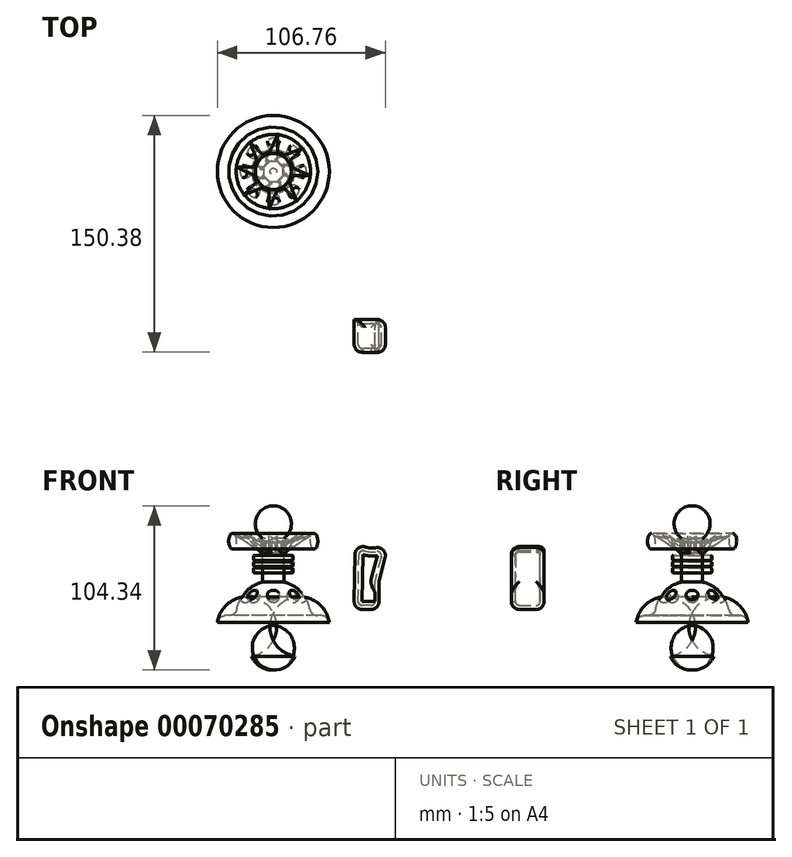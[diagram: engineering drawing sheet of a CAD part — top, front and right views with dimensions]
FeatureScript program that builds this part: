
annotation { "Feature Type Name" : "Feature", "Feature Type Description" : "" }
export const myFeature = defineFeature(function(context is Context, id is Id, definition is map)
    precondition{}
    {
        {
            var Q0;
            Q0=qCreatedBy(makeId("Front.planeOp"),FACE);
            var sketch = newSketch(context, id + "F0", { "sketchPlane" : qUnion([Q0])});
            skLineSegment(sketch, "E0", {"start": v(0, 56) * mm, "end": v(6.7, 56) * mm});
            skLineSegment(sketch, "E1", {"start": v(6.7, 56) * mm, "end": v(6.7, 21.36) * mm});
            skArc(sketch, "E2", {"start": v(23.55, 0) * mm, "mid": v(18.85, 13.62) * mm, "end": v(6.7, 21.36) * mm});
            skLineSegment(sketch, "E3", {"start": v(23.55, 0) * mm, "end": v(34.4, 0) * mm});
            skArc(sketch, "E4", {"start": v(13.85, -25.75) * mm, "mid": v(31.62, -18.85) * mm, "end": v(34.4, 0) * mm});
            skArc(sketch, "E5", {"start": v(0, -34.52) * mm, "mid": v(8.33, -32.35) * mm, "end": v(13.85, -25.75) * mm});
            skLineSegment(sketch, "E6", {"start": v(0, 54.15) * mm, "end": v(0, -34.52) * mm});
            skLineSegment(sketch, "E7", {"start": v(0, 54.15) * mm, "end": v(0, 56) * mm});
            skSolve(sketch);
        }
        {
            var Q0;
            Q0=makeQuery(id+"F0.imprint","IMPRINT",FACE,{"disambiguationData":[TD([[makeQuery(id+"F0.imprint","IMPRINT",EDGE,{"derivedFrom":sQuery(id+"F0.wireOp",EDGE,"E0")}),-1.0]])]});
            var Q1;
            Q1=sQuery(id+"F0.wireOp",EDGE,"E6");
            revolve(context, id + "F1", {"entities" : qUnion([Q0]), "axis" : qUnion([Q1]), "revolveType" : RevolveType.FULL});
        }
        {
            var Q0;
            Q0=makeQuery(id+"F1.opRevolve","SWEPT_EDGE",EDGE,{"disambiguationData":[OSD([sQuery(id+"F0.wireOp",EDGE,"E2"),sQuery(id+"F0.wireOp",EDGE,"E3")])]});
            var Q1;
            Q1=makeQuery(id+"F1.opRevolve","SWEPT_EDGE",EDGE,{"disambiguationData":[OSD([sQuery(id+"F0.wireOp",EDGE,"E3"),sQuery(id+"F0.wireOp",EDGE,"E4")])]});
            fillet(context, id + "F2", {"entities" : qUnion([Q0, Q1]), "radius" : 5.08 * mm, "tangentPropagation" : true, "allowEdgeOverflow" : false});
        }
        {
            var Q0;
            Q0=qCreatedBy(makeId("Front.planeOp"),FACE);
            cPlane(context, id + "F3", {"entities" : qUnion([Q0]), "cplaneType" : CPlaneType.OFFSET, "offset" : 76.2 * mm, "width" : 152.4 * mm, "height" : 152.4 * mm});
        }
        {
            var Q0;
            Q0=qCreatedBy(id+"F3.planeOp",FACE);
            var sketch = newSketch(context, id + "F4", { "sketchPlane" : qUnion([Q0])});
            skCircle(sketch, "E8", {"center": v(0, 12.35) * mm, "radius": 4.03 * mm});
            skLineSegment(sketch, "E9", {"start": v(0, 16.39) * mm, "end": v(0, 8.32) * mm});
            skSolve(sketch);
        }
        {
            var Q0;
            {var subQ0=sQuery(id+"F4.wireOp",EDGE,"E9");Q0=makeQuery(id+"F4.imprint","IMPRINT",FACE,{"disambiguationData":[TD([[makeQuery(id+"F4.imprint","IMPRINT",EDGE,{"derivedFrom":subQ0}),1.0]])]});}
            var Q1;
            Q1=sQuery(id+"F4.wireOp",EDGE,"E9");
            revolve(context, id + "F5", {"entities" : qUnion([Q0]), "axis" : qUnion([Q1]), "revolveType" : RevolveType.FULL});
        }
        {
            var Q0;
            Q0=makeQuery(id+"F5.opRevolve","SWEPT_BODY",BODY,{"disambiguationData":[OSD([sQuery(id+"F4.wireOp",EDGE,"E8"),sQuery(id+"F4.wireOp",EDGE,"E9")])]});
            transform(context, id + "F6", {"entities" : qUnion([Q0]), "transformType" : TransformType.TRANSLATION_3D, "dx" : 0 * mm, "dy" : 58.43 * mm, "dz" : 0 * mm, "makeCopy" : false});
        }
        {
            var Q0;
            Q0=qCreatedBy(makeId("Top.planeOp"),FACE);
            cPlane(context, id + "F7", {"entities" : qUnion([Q0]), "cplaneType" : CPlaneType.OFFSET, "offset" : 152.4 * mm, "width" : 152.4 * mm, "height" : 152.4 * mm});
        }
        {
            var Q0;
            Q0=qCreatedBy(id+"F7.planeOp",FACE);
            var sketch = newSketch(context, id + "F8", { "sketchPlane" : qUnion([Q0])});
            skCircle(sketch, "E10", {"center": v(0, 0) * mm, "radius": 11.45 * mm});
            skLineSegment(sketch, "E11", {"start": v(0, 11.45) * mm, "end": v(0, -11.45) * mm});
            skSolve(sketch);
        }
        {
            var Q0;
            {var subQ0=sQuery(id+"F8.wireOp",EDGE,"E11");Q0=makeQuery(id+"F8.imprint","IMPRINT",FACE,{"disambiguationData":[TD([[makeQuery(id+"F8.imprint","IMPRINT",EDGE,{"derivedFrom":subQ0}),1.0]])]});}
            var Q1;
            Q1=sQuery(id+"F8.wireOp",EDGE,"E11");
            revolve(context, id + "F9", {"entities" : qUnion([Q0]), "axis" : qUnion([Q1]), "revolveType" : RevolveType.FULL});
        }
        {
            var Q0;
            Q0=makeQuery(id+"F9.opRevolve","SWEPT_BODY",BODY,{"disambiguationData":[OSD([sQuery(id+"F8.wireOp",EDGE,"E10"),sQuery(id+"F8.wireOp",EDGE,"E11")])]});
            transform(context, id + "F10", {"entities" : qUnion([Q0]), "transformType" : TransformType.TRANSLATION_3D, "dx" : 0 * mm, "dy" : 0 * mm, "dz" : -94.04 * mm, "makeCopy" : false});
        }
        {
            var Q0;
            Q0=makeQuery(id+"F9.opRevolve","SWEPT_BODY",BODY,{"disambiguationData":[OSD([sQuery(id+"F8.wireOp",EDGE,"E10"),sQuery(id+"F8.wireOp",EDGE,"E11")])]});
            var Q1;
            Q1=makeQuery(id+"F1.opRevolve","SWEPT_BODY",BODY,{"disambiguationData":[OSD([sQuery(id+"F0.wireOp",EDGE,"E0"),sQuery(id+"F0.wireOp",EDGE,"E1"),sQuery(id+"F0.wireOp",EDGE,"E2"),sQuery(id+"F0.wireOp",EDGE,"E3"),sQuery(id+"F0.wireOp",EDGE,"E4"),sQuery(id+"F0.wireOp",EDGE,"E5"),sQuery(id+"F0.wireOp",EDGE,"E6"),sQuery(id+"F0.wireOp",EDGE,"E7")])]});
            booleanBodies(context, id + "F11", {"operationType" : BooleanOperationType.UNION, "tools" : qUnion([Q0, Q1])});
        }
        {
            var Q0;
            Q0=makeQuery(id+"F5.opRevolve","SWEPT_BODY",BODY,{"disambiguationData":[OSD([sQuery(id+"F4.wireOp",EDGE,"E8"),sQuery(id+"F4.wireOp",EDGE,"E9")])]});
            var Q1;
            Q1=makeQuery(id+"F1.opRevolve","SWEPT_EDGE",EDGE,{"disambiguationData":[OSD([sQuery(id+"F0.wireOp",EDGE,"E1"),sQuery(id+"F0.wireOp",EDGE,"E2")])]});
            circularPattern(context, id + "F12", {"entities" : qUnion([Q0]), "axis" : qUnion([Q1]), "angle" : 360 * degree, "instanceCount" : 8, "equalSpace" : true});
        }
        {
            var Q0;
            Q0=makeQuery(id+"F5.opRevolve","SWEPT_BODY",BODY,{"disambiguationData":[OSD([sQuery(id+"F4.wireOp",EDGE,"E8"),sQuery(id+"F4.wireOp",EDGE,"E9")])]});
            var Q1;
            Q1=makeQuery(id+"F9.opRevolve","SWEPT_BODY",BODY,{"disambiguationData":[OSD([sQuery(id+"F8.wireOp",EDGE,"E10"),sQuery(id+"F8.wireOp",EDGE,"E11")])]});
            booleanBodies(context, id + "F13", {"operationType" : BooleanOperationType.SUBTRACTION, "tools" : qUnion([Q0]), "targets" : qUnion([Q1])});
        }
        {
            var Q0;
            Q0=makeQuery(id+"F12.opPattern","COPY",BODY,{"derivedFrom":makeQuery(id+"F5.opRevolve","SWEPT_BODY",BODY,{"disambiguationData":[OSD([sQuery(id+"F4.wireOp",EDGE,"E8"),sQuery(id+"F4.wireOp",EDGE,"E9")])]}),"instanceName":"1"});
            var Q1;
            Q1=makeQuery(id+"F9.opRevolve","SWEPT_BODY",BODY,{"disambiguationData":[OSD([sQuery(id+"F8.wireOp",EDGE,"E10"),sQuery(id+"F8.wireOp",EDGE,"E11")])]});
            booleanBodies(context, id + "F14", {"operationType" : BooleanOperationType.SUBTRACTION, "tools" : qUnion([Q0]), "targets" : qUnion([Q1])});
        }
        {
            var Q0;
            Q0=makeQuery(id+"F12.opPattern","COPY",BODY,{"derivedFrom":makeQuery(id+"F5.opRevolve","SWEPT_BODY",BODY,{"disambiguationData":[OSD([sQuery(id+"F4.wireOp",EDGE,"E8"),sQuery(id+"F4.wireOp",EDGE,"E9")])]}),"instanceName":"2"});
            var Q1;
            Q1=makeQuery(id+"F9.opRevolve","SWEPT_BODY",BODY,{"disambiguationData":[OSD([sQuery(id+"F8.wireOp",EDGE,"E10"),sQuery(id+"F8.wireOp",EDGE,"E11")])]});
            booleanBodies(context, id + "F15", {"operationType" : BooleanOperationType.SUBTRACTION, "tools" : qUnion([Q0]), "targets" : qUnion([Q1])});
        }
        {
            var Q0;
            Q0=makeQuery(id+"F12.opPattern","COPY",BODY,{"derivedFrom":makeQuery(id+"F5.opRevolve","SWEPT_BODY",BODY,{"disambiguationData":[OSD([sQuery(id+"F4.wireOp",EDGE,"E8"),sQuery(id+"F4.wireOp",EDGE,"E9")])]}),"instanceName":"3"});
            var Q1;
            Q1=makeQuery(id+"F12.opPattern","COPY",BODY,{"derivedFrom":makeQuery(id+"F5.opRevolve","SWEPT_BODY",BODY,{"disambiguationData":[OSD([sQuery(id+"F4.wireOp",EDGE,"E8"),sQuery(id+"F4.wireOp",EDGE,"E9")])]}),"instanceName":"4"});
            var Q2;
            Q2=makeQuery(id+"F12.opPattern","COPY",BODY,{"derivedFrom":makeQuery(id+"F5.opRevolve","SWEPT_BODY",BODY,{"disambiguationData":[OSD([sQuery(id+"F4.wireOp",EDGE,"E8"),sQuery(id+"F4.wireOp",EDGE,"E9")])]}),"instanceName":"5"});
            var Q3;
            Q3=makeQuery(id+"F12.opPattern","COPY",BODY,{"derivedFrom":makeQuery(id+"F5.opRevolve","SWEPT_BODY",BODY,{"disambiguationData":[OSD([sQuery(id+"F4.wireOp",EDGE,"E8"),sQuery(id+"F4.wireOp",EDGE,"E9")])]}),"instanceName":"6"});
            var Q4;
            Q4=makeQuery(id+"F12.opPattern","COPY",BODY,{"derivedFrom":makeQuery(id+"F5.opRevolve","SWEPT_BODY",BODY,{"disambiguationData":[OSD([sQuery(id+"F4.wireOp",EDGE,"E8"),sQuery(id+"F4.wireOp",EDGE,"E9")])]}),"instanceName":"7"});
            var Q5;
            Q5=makeQuery(id+"F9.opRevolve","SWEPT_BODY",BODY,{"disambiguationData":[OSD([sQuery(id+"F8.wireOp",EDGE,"E10"),sQuery(id+"F8.wireOp",EDGE,"E11")])]});
            booleanBodies(context, id + "F16", {"operationType" : BooleanOperationType.SUBTRACTION, "tools" : qUnion([Q0, Q1, Q2, Q3, Q4]), "targets" : qUnion([Q5])});
        }
        {
            var Q0;
            Q0=qCreatedBy(makeId("Front.planeOp"),FACE);
            var sketch = newSketch(context, id + "F17", { "sketchPlane" : qUnion([Q0])});
            skEllipse(sketch, "E12", {"center": v(-25.95, 47.27) * mm, "majorRadius": 2.35 * mm, "minorRadius": 4.94 * mm, "majorAxis": v(1, 0)});
            skSolve(sketch);
        }
        {
            var Q0;
            Q0=makeQuery(id+"F17.imprint","IMPRINT",FACE,{"disambiguationData":[TD([[makeQuery(id+"F17.imprint","IMPRINT",EDGE,{"derivedFrom":sQuery(id+"F17.wireOp",EDGE,"E12")}),1.0]])]});
            var Q1;
            Q1=makeQuery(id+"F11.opBoolean","INTERSECT",EDGE,{"derivedFrom":[makeQuery(id+"F1.opRevolve","SWEPT_FACE",FACE,{"disambiguationData":[OSD([sQuery(id+"F0.wireOp",EDGE,"E1")])]}),makeQuery(id+"F9.opRevolve","SWEPT_FACE",FACE,{"disambiguationData":[OSD([sQuery(id+"F8.wireOp",EDGE,"E10")])]})]});
            sweep(context, id + "F18", {"profiles" : qUnion([Q0]), "path" : qUnion([Q1])});
        }
        {
            var Q0;
            Q0=qCreatedBy(makeId("Front.planeOp"),FACE);
            var sketch = newSketch(context, id + "F19", { "sketchPlane" : qUnion([Q0])});
            skEllipse(sketch, "E13", {"center": v(-12.17, 36.73) * mm, "majorRadius": 1.54 * mm, "minorRadius": 0.39 * mm, "majorAxis": v(0, 1)});
            skSolve(sketch);
        }
        {
            var Q0;
            Q0=makeQuery(id+"F19.imprint","IMPRINT",FACE,{"disambiguationData":[TD([[makeQuery(id+"F19.imprint","IMPRINT",EDGE,{"derivedFrom":sQuery(id+"F19.wireOp",EDGE,"E13")}),1.0]])]});
            var Q1;
            Q1=makeQuery(id+"F1.opRevolve","SWEPT_EDGE",EDGE,{"disambiguationData":[OSD([sQuery(id+"F0.wireOp",EDGE,"E1"),sQuery(id+"F0.wireOp",EDGE,"E2")])]});
            sweep(context, id + "F20", {"profiles" : qUnion([Q0]), "path" : qUnion([Q1])});
        }
        {
            var Q0;
            Q0=makeQuery(id+"F20.opSweep","SWEPT_BODY",BODY,{"disambiguationData":[OSD([sQuery(id+"F0.wireOp",EDGE,"E1"),sQuery(id+"F0.wireOp",EDGE,"E2"),sQuery(id+"F19.wireOp",EDGE,"E13")])]});
            transform(context, id + "F21", {"entities" : qUnion([Q0]), "transformType" : TransformType.COPY});
        }
        {
            var Q0;
            Q0=makeQuery(id+"F20.opSweep","SWEPT_BODY",BODY,{"disambiguationData":[OSD([sQuery(id+"F0.wireOp",EDGE,"E1"),sQuery(id+"F0.wireOp",EDGE,"E2"),sQuery(id+"F19.wireOp",EDGE,"E13")])]});
            transform(context, id + "F22", {"entities" : qUnion([Q0]), "transformType" : TransformType.TRANSLATION_3D, "dx" : 0 * mm, "dy" : 0 * mm, "dz" : -4 * mm, "makeCopy" : false});
        }
        {
            var Q0;
            Q0=makeQuery(id+"F20.opSweep","SWEPT_BODY",BODY,{"disambiguationData":[OSD([sQuery(id+"F0.wireOp",EDGE,"E1"),sQuery(id+"F0.wireOp",EDGE,"E2"),sQuery(id+"F19.wireOp",EDGE,"E13")])]});
            transform(context, id + "F23", {"entities" : qUnion([Q0]), "transformType" : TransformType.COPY});
        }
        {
            var Q0;
            Q0=makeQuery(id+"F20.opSweep","SWEPT_BODY",BODY,{"disambiguationData":[OSD([sQuery(id+"F0.wireOp",EDGE,"E1"),sQuery(id+"F0.wireOp",EDGE,"E2"),sQuery(id+"F19.wireOp",EDGE,"E13")])]});
            transform(context, id + "F24", {"entities" : qUnion([Q0]), "transformType" : TransformType.TRANSLATION_3D, "dx" : 0 * mm, "dy" : 0 * mm, "dz" : -4 * mm, "makeCopy" : false});
        }
        {
            var Q0;
            Q0=qCreatedBy(id+"F3.planeOp",FACE);
            var sketch = newSketch(context, id + "F25", { "sketchPlane" : qUnion([Q0])});
            skLineSegment(sketch, "E14.bottom", {"start": v(-56.72, 59.43) * mm, "end": v(-49.23, 59.43) * mm});
            skLineSegment(sketch, "E14.top", {"start": v(-56.72, 52.86) * mm, "end": v(-49.23, 52.86) * mm});
            skLineSegment(sketch, "E14.left", {"start": v(-56.72, 59.43) * mm, "end": v(-56.72, 52.86) * mm});
            skLineSegment(sketch, "E14.right", {"start": v(-49.23, 59.43) * mm, "end": v(-49.23, 52.86) * mm});
            skSolve(sketch);
        }
        {
            var Q0;
            Q0=qCreatedBy(id+"F3.planeOp",FACE);
            cPlane(context, id + "F26", {"entities" : qUnion([Q0]), "cplaneType" : CPlaneType.OFFSET, "offset" : 17.78 * mm, "width" : 152.4 * mm, "height" : 152.4 * mm});
        }
        {
            var Q0;
            Q0=qCreatedBy(id+"F26.planeOp",FACE);
            var sketch = newSketch(context, id + "F27", { "sketchPlane" : qUnion([Q0])});
            skPoint(sketch, "E15", {"position": v(-56.72, 63.62) * mm});
            skSolve(sketch);
        }
        {
            var Q0;
            Q0=makeQuery(id+"F25.imprint","IMPRINT",FACE,{"disambiguationData":[TD([[makeQuery(id+"F25.imprint","IMPRINT",EDGE,{"derivedFrom":sQuery(id+"F25.wireOp",EDGE,"E14.bottom")}),-1.0]])]});
            var Q1;
            Q1=sQuery(id+"F27.wireOp",VERTEX,"E15");
            loft(context, id + "F28", {"startCondition" : LoftEndDerivativeType.NORMAL_TO_PROFILE, "startMagnitude" : .2, "endCondition" : LoftEndDerivativeType.NORMAL_TO_PROFILE, "endMagnitude" : .2, "sheetProfilesArray" : [{ "sheetProfileEntities" : qUnion([Q0]) }, { "sheetProfileEntities" : qUnion([Q1]) }]});
        }
        {
            var Q0;
            Q0=makeQuery(id+"F28.opLoft","SWEPT_BODY",BODY,{"disambiguationData":[OSD([makeQuery(id+"F25.imprint","IMPRINT",FACE,{"disambiguationData":[TD([[makeQuery(id+"F25.imprint","IMPRINT",EDGE,{"derivedFrom":sQuery(id+"F25.wireOp",EDGE,"E14.bottom")}),-1.0]])]}),sQuery(id+"F27.wireOp",VERTEX,"E15")])]});
            transform(context, id + "F29", {"entities" : qUnion([Q0]), "transformType" : TransformType.TRANSLATION_3D, "dx" : 54.03 * mm, "dy" : 69.97 * mm, "dz" : -12.97 * mm, "makeCopy" : false});
        }
        {
            var Q0;
            Q0=makeQuery(id+"F28.opLoft","SWEPT_BODY",BODY,{"disambiguationData":[OSD([makeQuery(id+"F25.imprint","IMPRINT",FACE,{"disambiguationData":[TD([[makeQuery(id+"F25.imprint","IMPRINT",EDGE,{"derivedFrom":sQuery(id+"F25.wireOp",EDGE,"E14.bottom")}),-1.0]])]}),sQuery(id+"F27.wireOp",VERTEX,"E15")])]});
            var Q1;
            Q1=makeQuery(id+"F11.opBoolean","INTERSECT",EDGE,{"derivedFrom":[makeQuery(id+"F1.opRevolve","SWEPT_FACE",FACE,{"disambiguationData":[OSD([sQuery(id+"F0.wireOp",EDGE,"E1")])]}),makeQuery(id+"F9.opRevolve","SWEPT_FACE",FACE,{"disambiguationData":[OSD([sQuery(id+"F8.wireOp",EDGE,"E10")])]})]});
            circularPattern(context, id + "F30", {"entities" : qUnion([Q0]), "axis" : qUnion([Q1]), "angle" : 360 * degree, "instanceCount" : 8, "equalSpace" : true});
        }
        {
            var Q0;
            Q0=qCreatedBy(id+"F26.planeOp",FACE);
            var sketch = newSketch(context, id + "F31", { "sketchPlane" : qUnion([Q0])});
            skArc(sketch, "E16", {"start": v(51.95, 47.28) * mm, "mid": v(62.86, 42.96) * mm, "end": v(73.78, 47.28) * mm});
            skLineSegment(sketch, "E17", {"start": v(73.78, 47.28) * mm, "end": v(67.2, 22.34) * mm});
            skLineSegment(sketch, "E18", {"start": v(67.2, 22.34) * mm, "end": v(67.2, 3.98) * mm});
            skLineSegment(sketch, "E19", {"start": v(67.2, 3.98) * mm, "end": v(51.26, 3.98) * mm});
            skLineSegment(sketch, "E20", {"start": v(51.26, 3.98) * mm, "end": v(51.95, 47.28) * mm});
            skSolve(sketch);
        }
        {
            var Q0;
            Q0=makeQuery(id+"F31.imprint","IMPRINT",FACE,{"disambiguationData":[TD([[makeQuery(id+"F31.imprint","IMPRINT",EDGE,{"derivedFrom":sQuery(id+"F31.wireOp",EDGE,"E16")}),-1.0]])]});
            extrude(context, id + "F32", {"entities" : qUnion([Q0]), "depth" : 20.83 * mm});
        }
        {
            var Q0;
            Q0=makeQuery(id+"F32.opExtrude","SWEPT_FACE",FACE,{"disambiguationData":[OSD([sQuery(id+"F31.wireOp",EDGE,"E17")])]});
            var Q1;
            Q1=makeQuery(id+"F32.opExtrude","SWEPT_FACE",FACE,{"disambiguationData":[OSD([sQuery(id+"F31.wireOp",EDGE,"E19")])]});
            var Q2;
            Q2=makeQuery(id+"F32.opExtrude","SWEPT_FACE",FACE,{"disambiguationData":[OSD([sQuery(id+"F31.wireOp",EDGE,"E16")])]});
            var Q3;
            Q3=makeQuery(id+"F32.opExtrude","CAP_EDGE",EDGE,{"disambiguationData":[OSD([sQuery(id+"F31.wireOp",EDGE,"E20")])],"isStart":false});
            fillet(context, id + "F33", {"entities" : qUnion([Q0, Q1, Q2, Q3]), "radius" : 5.08 * mm, "tangentPropagation" : true, "allowEdgeOverflow" : false});
        }
        {
            var Q0;
            Q0=makeQuery(id+"F32.opExtrude","CAP_FACE",FACE,{"disambiguationData":[OSD([sQuery(id+"F31.wireOp",EDGE,"E16"),sQuery(id+"F31.wireOp",EDGE,"E17"),sQuery(id+"F31.wireOp",EDGE,"E18"),sQuery(id+"F31.wireOp",EDGE,"E19"),sQuery(id+"F31.wireOp",EDGE,"E20")])],"isStart":false});
            shell(context, id + "F34", {"entities" : qUnion([Q0]), "thickness" : 2.54 * mm});
        }
    });
